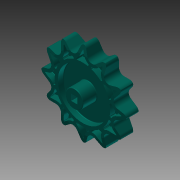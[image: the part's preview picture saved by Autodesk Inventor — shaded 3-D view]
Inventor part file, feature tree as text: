
AUTODESK INVENTOR PART (.ipt)
format: ipt  version: 2013 (Build 170138000, 138)  size: 1,382,400 bytes
history: native  units: in
note: dims shown in document units (in); Inventor stores cm internally (conversion verified against a paired STEP export)
features: sketch x6, extrude x6, fillet x2, revolve x1, pattern_circular x1, mirror x1, other x1
ambient origin geometry x8: Origin, YZ Plane, XZ Plane, XY Plane, X Axis, Y Axis, Z Axis, Center Point
bodies: Solid1 (feature_tree)
feature tree (18):
  sketch  "Sketch1"  dims[d0=0.3in d1=0.0in d2=0.984in]
  extrude  "Extrusion1"  Depth=0.984in
  extrude  "Extrusion2"  Depth=0.354in
  extrude  "Extrusion3"  Depth=0.012in
  fillet  "Fillet1"  [1 undecoded]
  revolve  "Revolution1"  [1 undecoded]
  extrude  "Extrusion4"  Depth=0.165in
  fillet  "Fillet2"  Radius=4.7244in
  pattern_circular  "Circular Pattern1"  [2 undecoded]
  mirror  "Mirror1"
  extrude  "Extrusion5"  TaperAngle=0.0deg  [1 undecoded]
  sketch  "Sketch2"  dims[d3=0.111in d4=0.0in d5=0.354in]
  sketch  "Sketch3"  dims[d6=0.273in d7=0.0in d8=0.012in d11=90.0deg]
  sketch  "Sketch4"  dims[d12=0.111in d13=0.0in d14=0.007in]
  sketch  "Sketch5"  dims[d15=0.029in d16=0.165in d17=4.7244in d18=360.0deg]
  sketch  "Sketch6"  dims[d20=0.111in d21=0.0in d22=0.389in d23=0.0in d24=0.0in d25=0.0in]
  other  "Srf1"
  extrude  "ExtrusionSrf1"  TaperAngle=0.0deg  [1 undecoded]
note: 6 required parameter values undecoded (feature->parameter linkage not recoverable at this tier; creation-order binding heuristic only, values carry confidence <= 0.55)